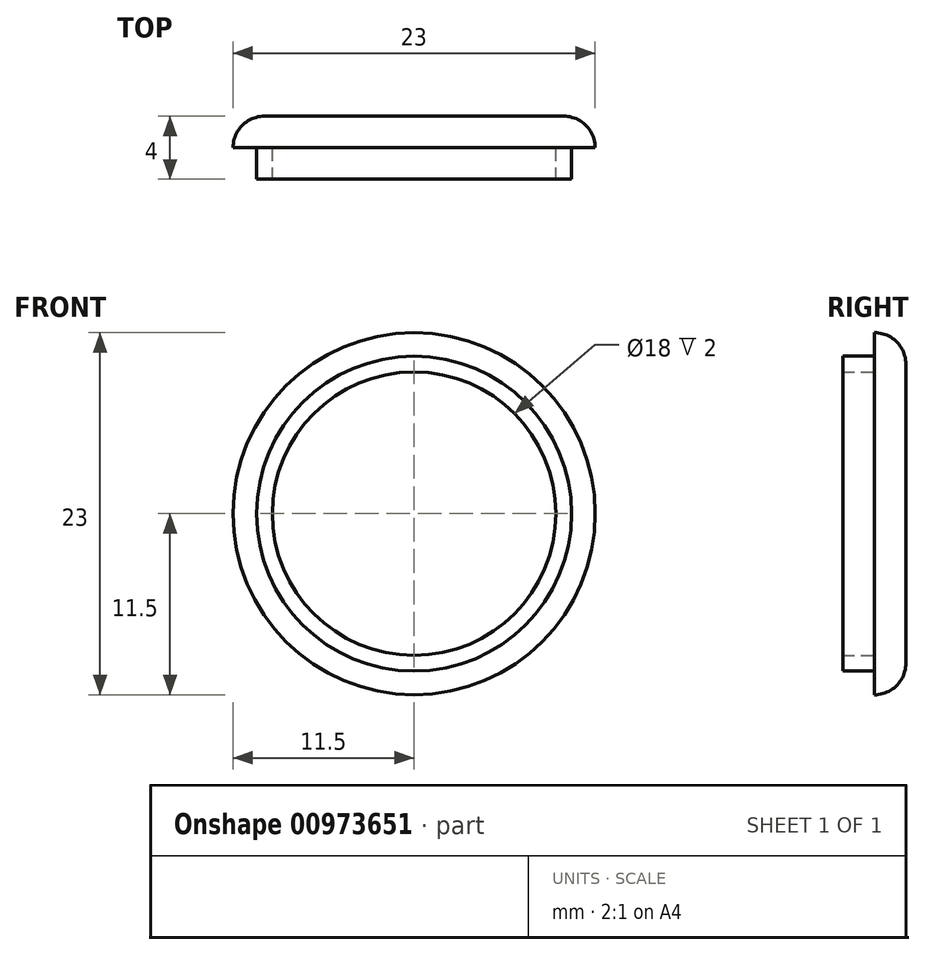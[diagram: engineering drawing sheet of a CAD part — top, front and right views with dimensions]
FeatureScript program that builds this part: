
annotation { "Feature Type Name" : "Feature", "Feature Type Description" : "" }
export const myFeature = defineFeature(function(context is Context, id is Id, definition is map)
    precondition{}
    {
        {
            var Q0;
            Q0=qCreatedBy(makeId("Front.planeOp"),FACE);
            var sketch = newSketch(context, id + "F0", { "sketchPlane" : qUnion([Q0])});
            skCircle(sketch, "E0", {"center": v(0, 0) * mm, "radius": 11.5 * mm});
            skSolve(sketch);
        }
        {
            var Q0;
            Q0=makeQuery(id+"F0.imprint","IMPRINT",FACE,{"disambiguationData":[TD([[makeQuery(id+"F0.imprint","IMPRINT",EDGE,{"derivedFrom":sQuery(id+"F0.wireOp",EDGE,"E0")}),1.0]])]});
            extrude(context, id + "F1", {"entities" : qUnion([Q0]), "depth" : 2 * mm, "offsetDistance" : 25 * mm});
        }
        {
            var Q0;
            Q0=makeQuery(id+"F1.opExtrude","CAP_FACE",FACE,{"disambiguationData":[OSD([sQuery(id+"F0.wireOp",EDGE,"E0")])],"isStart":false});
            var sketch = newSketch(context, id + "F2", { "sketchPlane" : qUnion([Q0])});
            skCircle(sketch, "E1", {"center": v(0, 0) * mm, "radius": 10 * mm});
            skCircle(sketch, "E2", {"center": v(0, 0) * mm, "radius": 9 * mm});
            skSolve(sketch);
        }
        {
            var Q0;
            Q0=makeQuery(id+"F2.imprint","IMPRINT",FACE,{"disambiguationData":[TD([[makeQuery(id+"F2.imprint","IMPRINT",EDGE,{"derivedFrom":sQuery(id+"F2.wireOp",EDGE,"E1")}),1.0]])]});
            var Q1;
            Q1=sQuery(id+"F2.wireOp",EDGE,"E1");
            extrude(context, id + "F3", {"entities" : qUnion([Q0]), "operationType" : NewBodyOperationType.ADD, "surfaceOperationType" : NewSurfaceOperationType.ADD, "surfaceEntities" : qUnion([Q1]), "depth" : 2 * mm, "offsetDistance" : 25 * mm});
        }
        {
            var Q0;
            Q0=makeQuery(id+"F1.opExtrude","CAP_EDGE",EDGE,{"disambiguationData":[OSD([sQuery(id+"F0.wireOp",EDGE,"E0")])],"isStart":true});
            fillet(context, id + "F4", {"entities" : qUnion([Q0]), "radius" : 2 * mm, "tangentPropagation" : true, "allowEdgeOverflow" : false});
        }
    });
